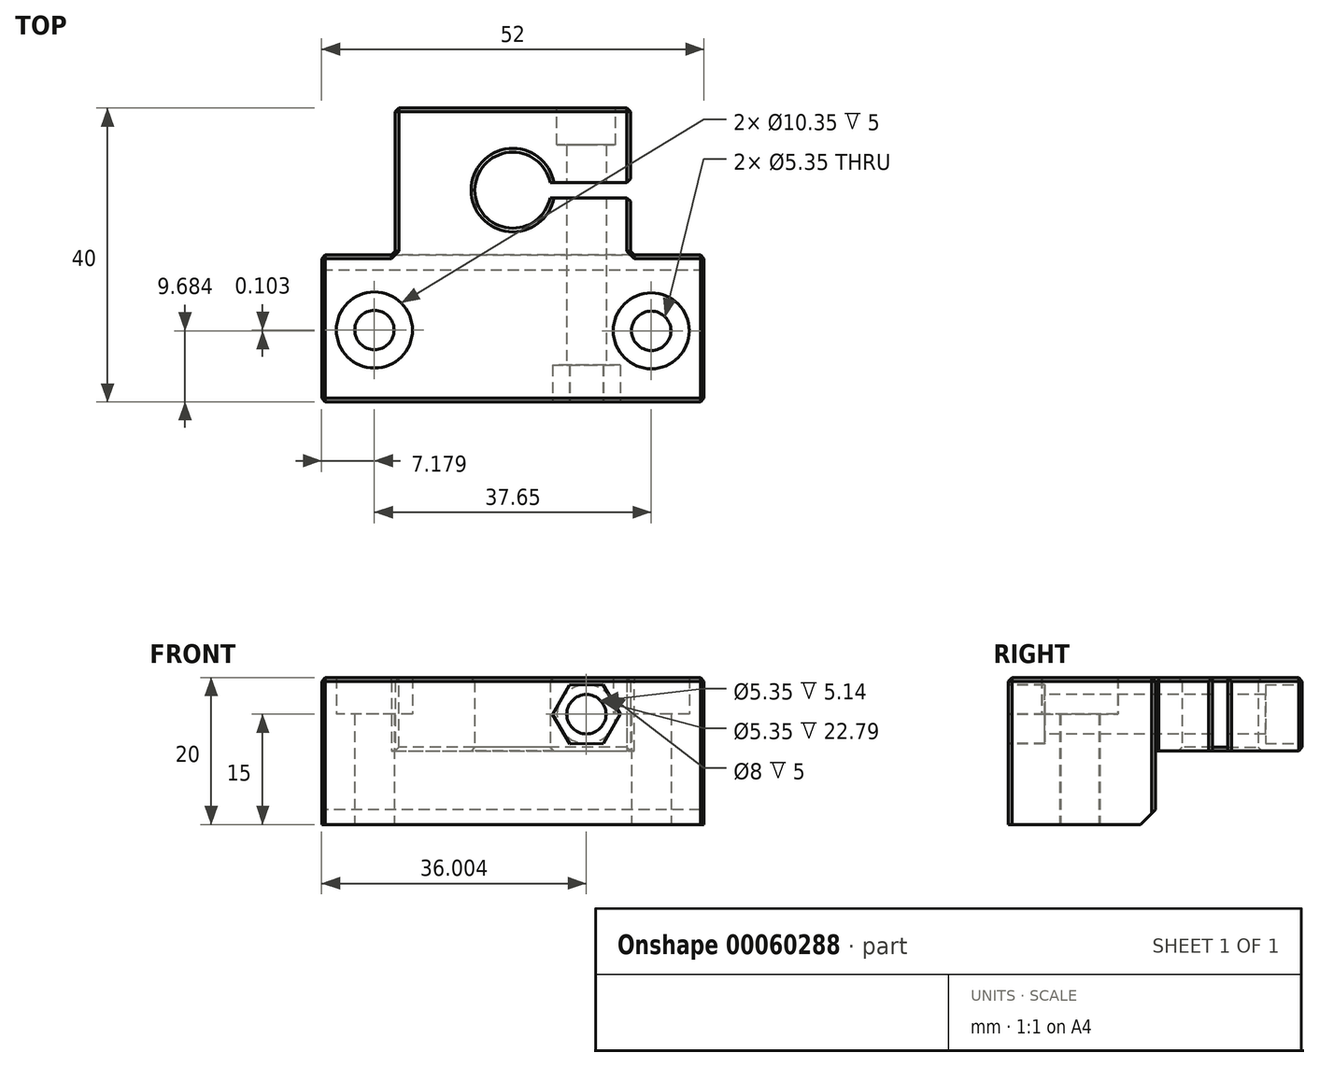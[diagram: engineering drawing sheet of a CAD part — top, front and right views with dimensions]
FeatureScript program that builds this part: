
annotation { "Feature Type Name" : "Feature", "Feature Type Description" : "" }
export const myFeature = defineFeature(function(context is Context, id is Id, definition is map)
    precondition{}
    {
        {
            var Q0;
            Q0=qCreatedBy(makeId("Top.planeOp"),FACE);
            var sketch = newSketch(context, id + "F0", { "sketchPlane" : qUnion([Q0])});
            skLineSegment(sketch, "E0.bottom", {"start": v(-17.08, 11.18) * mm, "end": v(14.92, 11.18) * mm});
            skLineSegment(sketch, "E0.left", {"start": v(-17.08, 11.18) * mm, "end": v(-17.08, -8.82) * mm});
            skLineSegment(sketch, "E0.right", {"start": v(14.92, 11.18) * mm, "end": v(14.92, 1.04) * mm});
            skArc(sketch, "E1", {"start": v(4, 1.04) * mm, "mid": v(-6.25, 0) * mm, "end": v(4, -1.04) * mm});
            skPoint(sketch, "E1.centerSnap0", {"position": v(-1.08, -9) * mm});
            skLineSegment(sketch, "E2", {"start": v(14.92, -1.04) * mm, "end": v(4, -1.04) * mm});
            skLineSegment(sketch, "E3", {"start": v(4, 1.04) * mm, "end": v(14.92, 1.04) * mm});
            skLineSegment(sketch, "E4.trimOffspring", {"start": v(14.92, -1.04) * mm, "end": v(14.92, -8.82) * mm});
            skLineSegment(sketch, "E5", {"start": v(-17.08, -28.83) * mm, "end": v(14.92, -28.82) * mm});
            skCircle(sketch, "E6", {"center": v(-19.9, -19.03) * mm, "radius": 2.67 * mm});
            skCircle(sketch, "E7", {"center": v(17.75, -19.14) * mm, "radius": 2.67 * mm});
            skPoint(sketch, "E8.start.orphan", {"position": v(-17.08, -18.83) * mm});
            skPoint(sketch, "E9.trimOffspring.end.orphan", {"position": v(14.92, -18.82) * mm});
            skLineSegment(sketch, "E10", {"start": v(14.92, -8.82) * mm, "end": v(24.92, -8.82) * mm});
            skLineSegment(sketch, "E11", {"start": v(24.92, -8.82) * mm, "end": v(24.92, -28.82) * mm});
            skLineSegment(sketch, "E12", {"start": v(24.92, -28.82) * mm, "end": v(14.92, -28.82) * mm});
            skCircle(sketch, "E13", {"center": v(-19.9, -19.03) * mm, "radius": 5.17 * mm});
            skCircle(sketch, "E14", {"center": v(17.75, -19.14) * mm, "radius": 5.17 * mm});
            skLineSegment(sketch, "E15", {"start": v(-17.08, -8.82) * mm, "end": v(-27.08, -8.82) * mm});
            skLineSegment(sketch, "E16", {"start": v(-27.08, -8.83) * mm, "end": v(-27.08, -28.83) * mm});
            skLineSegment(sketch, "E17", {"start": v(-27.08, -28.83) * mm, "end": v(-17.08, -28.83) * mm});
            skLineSegment(sketch, "E18", {"start": v(-17.08, -8.82) * mm, "end": v(14.92, -8.82) * mm});
            skSolve(sketch);
        }
        {
            var Q0;
            Q0 = qSketchRegion(id + "F0", true);
            extrude(context, id + "F1", {"entities" : qUnion([Q0]), "depth" : 10 * mm});
        }
        {
            var Q0;
            Q0=makeQuery(id+"F0.imprint","IMPRINT",FACE,{"disambiguationData":[TD([[makeQuery(id+"F0.imprint","IMPRINT",EDGE,{"derivedFrom":sQuery(id+"F0.wireOp",EDGE,"E6")}),-1.0]])]});
            extrude(context, id + "F2", {"entities" : qUnion([Q0]), "operationType" : NewBodyOperationType.ADD, "depth" : 5 * mm});
        }
        {
            var Q0;
            Q0=makeQuery(id+"F0.imprint","IMPRINT",FACE,{"disambiguationData":[TD([[makeQuery(id+"F0.imprint","IMPRINT",EDGE,{"derivedFrom":sQuery(id+"F0.wireOp",EDGE,"E7")}),-1.0]])]});
            extrude(context, id + "F3", {"entities" : qUnion([Q0]), "operationType" : NewBodyOperationType.ADD, "depth" : 5 * mm});
        }
        {
            var Q0;
            Q0=makeQuery(id+"F1.opExtrude","SWEPT_FACE",FACE,{"disambiguationData":[OSD([sQuery(id+"F0.wireOp",EDGE,"E5"),sQuery(id+"F0.wireOp",EDGE,"E12"),sQuery(id+"F0.wireOp",EDGE,"E17")])]});
            var sketch = newSketch(context, id + "F4", { "sketchPlane" : qUnion([Q0])});
            skCircle(sketch, "E19.cCircle", {"center": v(8.92, 5) * mm, "radius": 4 * mm, "construction": true});
            skLineSegment(sketch, "E19.0", {"start": v(6.64, 0.99) * mm, "end": v(4.3, 4.97) * mm});
            skLineSegment(sketch, "E19.1", {"start": v(4.3, 4.97) * mm, "end": v(6.59, 8.98) * mm});
            skLineSegment(sketch, "E19.2", {"start": v(6.59, 8.98) * mm, "end": v(11.2, 9.01) * mm});
            skLineSegment(sketch, "E19.3", {"start": v(11.2, 9.01) * mm, "end": v(13.54, 5.03) * mm});
            skLineSegment(sketch, "E19.4", {"start": v(13.54, 5.03) * mm, "end": v(11.26, 1.02) * mm});
            skLineSegment(sketch, "E19.5", {"start": v(11.26, 1.02) * mm, "end": v(6.64, 0.99) * mm});
            skPoint(sketch, "E19.0.midPoint", {"position": v(5.47, 2.98) * mm});
            skCircle(sketch, "E20", {"center": v(8.92, 5) * mm, "radius": 2.67 * mm});
            skSolve(sketch);
        }
        {
            var Q0;
            Q0=makeQuery(id+"F4.imprint","IMPRINT",FACE,{"disambiguationData":[TD([[makeQuery(id+"F4.imprint","IMPRINT",EDGE,{"derivedFrom":sQuery(id+"F4.wireOp",EDGE,"E20")}),1.0]])]});
            extrude(context, id + "F5", {"entities" : qUnion([Q0]), "operationType" : NewBodyOperationType.REMOVE, "oppositeDirection" : true, "depth" : 40 * mm});
        }
        {
            var Q0;
            Q0=makeQuery(id+"F4.imprint","IMPRINT",FACE,{"disambiguationData":[TD([[makeQuery(id+"F4.imprint","IMPRINT",EDGE,{"derivedFrom":sQuery(id+"F4.wireOp",EDGE,"E19.0")}),-1.0]])]});
            extrude(context, id + "F6", {"entities" : qUnion([Q0]), "operationType" : NewBodyOperationType.REMOVE, "oppositeDirection" : true, "depth" : 5 * mm});
        }
        {
            var Q0;
            Q0=makeQuery(id+"F1.opExtrude","SWEPT_FACE",FACE,{"disambiguationData":[OSD([sQuery(id+"F0.wireOp",EDGE,"E0.bottom")])]});
            var sketch = newSketch(context, id + "F7", { "sketchPlane" : qUnion([Q0])});
            skCircle(sketch, "E21", {"center": v(-8.92, 5) * mm, "radius": 4 * mm});
            skSolve(sketch);
        }
        {
            var Q0;
            Q0=makeQuery(id+"F7.imprint","IMPRINT",FACE,{"disambiguationData":[TD([[makeQuery(id+"F7.imprint","IMPRINT",EDGE,{"derivedFrom":sQuery(id+"F7.wireOp",EDGE,"E21")}),1.0]])]});
            extrude(context, id + "F8", {"entities" : qUnion([Q0]), "operationType" : NewBodyOperationType.REMOVE, "oppositeDirection" : true, "depth" : 5 * mm});
        }
        {
            var Q0;
            Q0=makeQuery(id+"F1.opExtrude","CAP_EDGE",EDGE,{"disambiguationData":[OSD([sQuery(id+"F0.wireOp",EDGE,"E16")])],"isStart":false});
            var Q1;
            Q1=makeQuery(id+"F1.opExtrude","CAP_EDGE",EDGE,{"disambiguationData":[OSD([sQuery(id+"F0.wireOp",EDGE,"E15")])],"isStart":false});
            var Q2;
            Q2=makeQuery(id+"F1.opExtrude","CAP_EDGE",EDGE,{"disambiguationData":[OSD([sQuery(id+"F0.wireOp",EDGE,"E0.left")])],"isStart":false});
            var Q3;
            Q3=makeQuery(id+"F1.opExtrude","CAP_EDGE",EDGE,{"disambiguationData":[OSD([sQuery(id+"F0.wireOp",EDGE,"E0.bottom")])],"isStart":false});
            var Q4;
            Q4=makeQuery(id+"F1.opExtrude","CAP_EDGE",EDGE,{"disambiguationData":[OSD([sQuery(id+"F0.wireOp",EDGE,"E0.right")])],"isStart":false});
            var Q5;
            Q5=makeQuery(id+"F1.opExtrude","CAP_EDGE",EDGE,{"disambiguationData":[OSD([sQuery(id+"F0.wireOp",EDGE,"E4.trimOffspring")])],"isStart":false});
            var Q6;
            Q6=makeQuery(id+"F1.opExtrude","CAP_EDGE",EDGE,{"disambiguationData":[OSD([sQuery(id+"F0.wireOp",EDGE,"E10")])],"isStart":false});
            var Q7;
            Q7=makeQuery(id+"F1.opExtrude","CAP_EDGE",EDGE,{"disambiguationData":[OSD([sQuery(id+"F0.wireOp",EDGE,"E11")])],"isStart":false});
            var Q8;
            Q8=makeQuery(id+"F1.opExtrude","SWEPT_EDGE",EDGE,{"disambiguationData":[OSD([sQuery(id+"F0.wireOp",EDGE,"E10"),sQuery(id+"F0.wireOp",EDGE,"E11")])]});
            var Q9;
            Q9=makeQuery(id+"F1.opExtrude","SWEPT_EDGE",EDGE,{"disambiguationData":[OSD([sQuery(id+"F0.wireOp",EDGE,"E4.trimOffspring"),sQuery(id+"F0.wireOp",EDGE,"E10")])]});
            var Q10;
            Q10=makeQuery(id+"F1.opExtrude","SWEPT_EDGE",EDGE,{"disambiguationData":[OSD([sQuery(id+"F0.wireOp",EDGE,"E2"),sQuery(id+"F0.wireOp",EDGE,"E4.trimOffspring")])]});
            var Q11;
            Q11=makeQuery(id+"F1.opExtrude","SWEPT_EDGE",EDGE,{"disambiguationData":[OSD([sQuery(id+"F0.wireOp",EDGE,"E0.right"),sQuery(id+"F0.wireOp",EDGE,"E3")])]});
            var Q12;
            Q12=makeQuery(id+"F1.opExtrude","SWEPT_EDGE",EDGE,{"disambiguationData":[OSD([sQuery(id+"F0.wireOp",EDGE,"E0.bottom"),sQuery(id+"F0.wireOp",EDGE,"E0.right")])]});
            var Q13;
            Q13=makeQuery(id+"F1.opExtrude","SWEPT_EDGE",EDGE,{"disambiguationData":[OSD([sQuery(id+"F0.wireOp",EDGE,"E0.bottom"),sQuery(id+"F0.wireOp",EDGE,"E0.left")])]});
            var Q14;
            Q14=makeQuery(id+"F1.opExtrude","SWEPT_EDGE",EDGE,{"disambiguationData":[OSD([sQuery(id+"F0.wireOp",EDGE,"E0.left"),sQuery(id+"F0.wireOp",EDGE,"E15")])]});
            var Q15;
            Q15=makeQuery(id+"F1.opExtrude","SWEPT_EDGE",EDGE,{"disambiguationData":[OSD([sQuery(id+"F0.wireOp",EDGE,"E15"),sQuery(id+"F0.wireOp",EDGE,"E16")])]});
            var Q16;
            Q16=makeQuery(id+"F1.opExtrude","SWEPT_EDGE",EDGE,{"disambiguationData":[OSD([sQuery(id+"F0.wireOp",EDGE,"E16"),sQuery(id+"F0.wireOp",EDGE,"E17")])]});
            var Q17;
            Q17=makeQuery(id+"F1.opExtrude","SWEPT_EDGE",EDGE,{"disambiguationData":[OSD([sQuery(id+"F0.wireOp",EDGE,"E11"),sQuery(id+"F0.wireOp",EDGE,"E12")])]});
            var Q18;
            Q18=makeQuery(id+"F1.opExtrude","CAP_EDGE",EDGE,{"disambiguationData":[OSD([sQuery(id+"F0.wireOp",EDGE,"E1")])],"isStart":false});
            var Q19;
            Q19=makeQuery(id+"F1.opExtrude","CAP_EDGE",EDGE,{"disambiguationData":[OSD([sQuery(id+"F0.wireOp",EDGE,"E5"),sQuery(id+"F0.wireOp",EDGE,"E12"),sQuery(id+"F0.wireOp",EDGE,"E17")])],"isStart":false});
            var Q20;
            Q20=makeQuery(id+"F1.opExtrude","CAP_EDGE",EDGE,{"disambiguationData":[OSD([sQuery(id+"F0.wireOp",EDGE,"E1")])],"isStart":true});
            var Q21;
            Q21=makeQuery(id+"F1.opExtrude","CAP_EDGE",EDGE,{"disambiguationData":[OSD([sQuery(id+"F0.wireOp",EDGE,"E0.bottom")])],"isStart":true});
            chamfer(context, id + "F9", {"entities" : qUnion([Q0, Q1, Q2, Q3, Q4, Q5, Q6, Q7, Q8, Q9, Q10, Q11, Q12, Q13, Q14, Q15, Q16, Q17, Q18, Q19, Q20, Q21]), "width" : 0.5 * mm, "tangentPropagation" : true});
        }
        {
            var Q0;
            Q0=makeQuery(id+"F0.imprint","IMPRINT",FACE,{"disambiguationData":[TD([[makeQuery(id+"F0.imprint","IMPRINT",EDGE,{"derivedFrom":sQuery(id+"F0.wireOp",EDGE,"E5")}),1.0]])]});
            extrude(context, id + "F10", {"entities" : qUnion([Q0]), "operationType" : NewBodyOperationType.ADD, "oppositeDirection" : true, "depth" : 10 * mm});
        }
        {
            var Q0;
            Q0=makeQuery(id+"F0.imprint","IMPRINT",FACE,{"disambiguationData":[TD([[makeQuery(id+"F0.imprint","IMPRINT",EDGE,{"derivedFrom":sQuery(id+"F0.wireOp",EDGE,"E7")}),-1.0]])]});
            var Q1;
            Q1=makeQuery(id+"F0.imprint","IMPRINT",FACE,{"disambiguationData":[TD([[makeQuery(id+"F0.imprint","IMPRINT",EDGE,{"derivedFrom":sQuery(id+"F0.wireOp",EDGE,"E6")}),-1.0]])]});
            extrude(context, id + "F11", {"entities" : qUnion([Q0, Q1]), "operationType" : NewBodyOperationType.ADD, "oppositeDirection" : true, "depth" : 10 * mm});
        }
        {
            var Q0;
            Q0=makeQuery(id+"F10.opExtrude","SWEPT_EDGE",EDGE,{"disambiguationData":[OSD([sQuery(id+"F0.wireOp",EDGE,"E10"),sQuery(id+"F0.wireOp",EDGE,"E11")])]});
            var Q1;
            Q1=makeQuery(id+"F10.opExtrude","SWEPT_EDGE",EDGE,{"disambiguationData":[OSD([sQuery(id+"F0.wireOp",EDGE,"E15"),sQuery(id+"F0.wireOp",EDGE,"E16")])]});
            var Q2;
            Q2=makeQuery(id+"F10.opExtrude","SWEPT_EDGE",EDGE,{"disambiguationData":[OSD([sQuery(id+"F0.wireOp",EDGE,"E11"),sQuery(id+"F0.wireOp",EDGE,"E12")])]});
            var Q3;
            Q3=makeQuery(id+"F10.opExtrude","SWEPT_EDGE",EDGE,{"disambiguationData":[OSD([sQuery(id+"F0.wireOp",EDGE,"E16"),sQuery(id+"F0.wireOp",EDGE,"E17")])]});
            chamfer(context, id + "F12", {"entities" : qUnion([Q0, Q1, Q2, Q3]), "width" : 0.5 * mm, "tangentPropagation" : true});
        }
        {
            var Q0;
            Q0=makeQuery(id+"F10.opExtrude","CAP_EDGE",EDGE,{"disambiguationData":[OSD([sQuery(id+"F0.wireOp",EDGE,"E10"),sQuery(id+"F0.wireOp",EDGE,"E15"),sQuery(id+"F0.wireOp",EDGE,"E18")])],"isStart":false});
            chamfer(context, id + "F13", {"entities" : qUnion([Q0]), "width" : 2 * mm, "tangentPropagation" : true});
        }
    });
